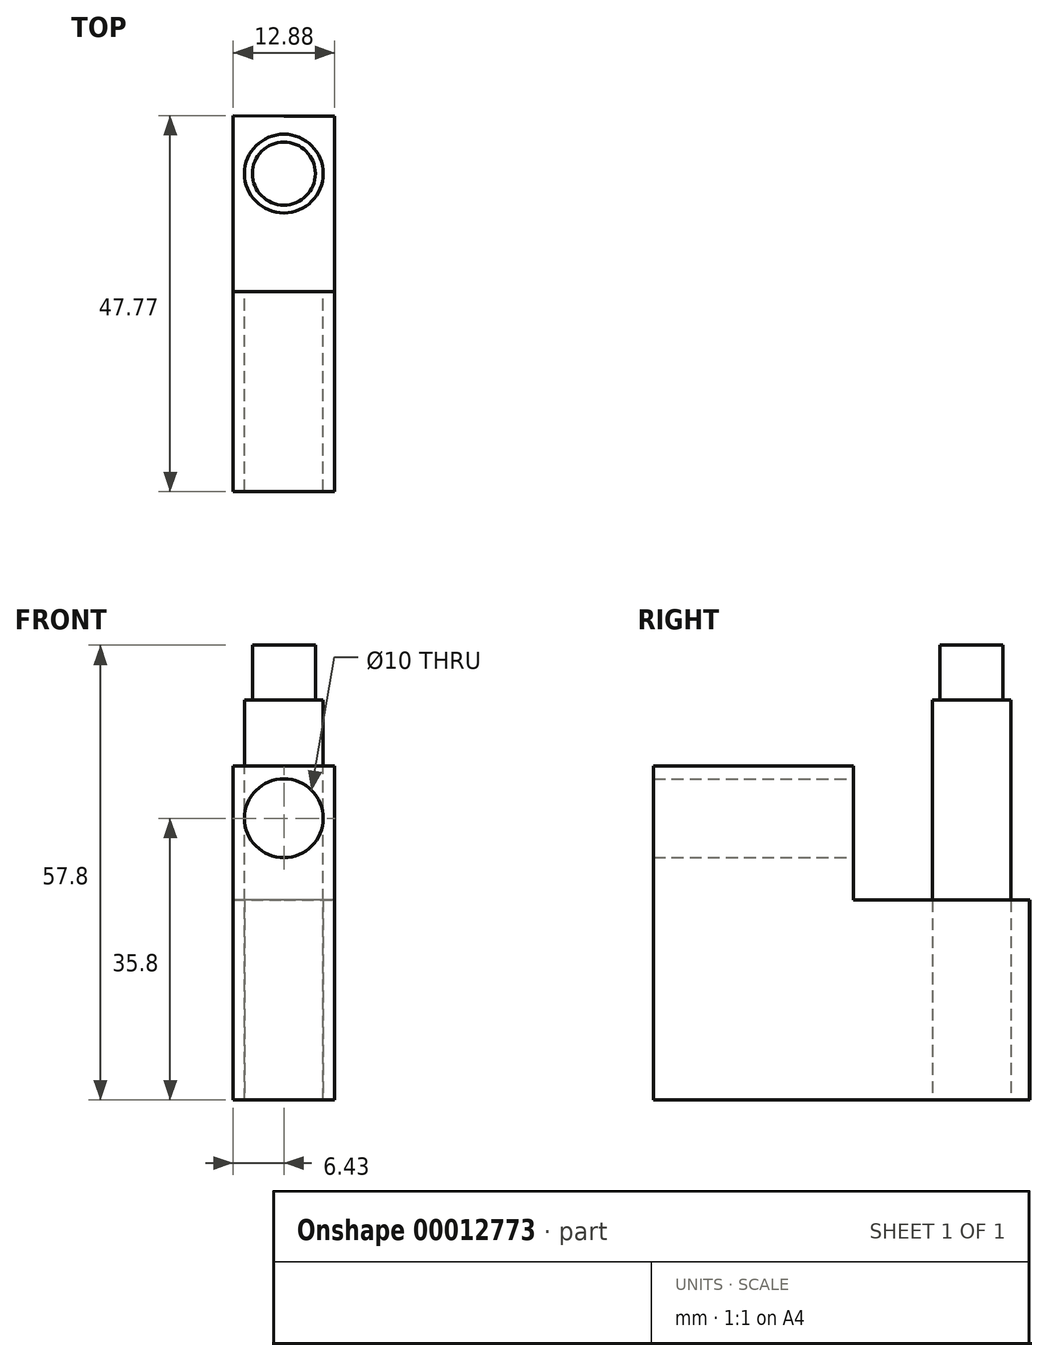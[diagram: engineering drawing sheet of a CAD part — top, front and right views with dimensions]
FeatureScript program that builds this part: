
annotation { "Feature Type Name" : "Feature", "Feature Type Description" : "" }
export const myFeature = defineFeature(function(context is Context, id is Id, definition is map)
    precondition{}
    {
        {
            var Q0;
            Q0=qCreatedBy(makeId("Top.planeOp"),FACE);
            var sketch = newSketch(context, id + "F0", { "sketchPlane" : qUnion([Q0])});
            skCircle(sketch, "E0", {"center": v(0, 0) * mm, "radius": 4 * mm});
            skSolve(sketch);
        }
        {
            var Q0;
            Q0=makeQuery(id+"F0.imprint","IMPRINT",FACE,{"disambiguationData":[TD([[makeQuery(id+"F0.imprint","IMPRINT",EDGE,{"derivedFrom":sQuery(id+"F0.wireOp",EDGE,"E0")}),1.0]])]});
            extrude(context, id + "F1", {"entities" : qUnion([Q0]), "depth" : 7 * mm});
        }
        {
            var Q0;
            Q0=qCreatedBy(makeId("Top.planeOp"),FACE);
            var sketch = newSketch(context, id + "F2", { "sketchPlane" : qUnion([Q0])});
            skCircle(sketch, "E1", {"center": v(0, 0) * mm, "radius": 5 * mm});
            skSolve(sketch);
        }
        {
            var Q0;
            Q0=makeQuery(id+"F2.imprint","IMPRINT",FACE,{"disambiguationData":[TD([[makeQuery(id+"F2.imprint","IMPRINT",EDGE,{"derivedFrom":sQuery(id+"F2.wireOp",EDGE,"E1")}),1.0]])]});
            extrude(context, id + "F3", {"entities" : qUnion([Q0]), "operationType" : NewBodyOperationType.ADD, "oppositeDirection" : true, "depth" : 50.8 * mm});
        }
        {
            var Q0;
            Q0=makeQuery(id+"F3.opExtrude","CAP_FACE",FACE,{"disambiguationData":[OSD([sQuery(id+"F2.wireOp",EDGE,"E1")])],"isStart":false});
            var sketch = newSketch(context, id + "F4", { "sketchPlane" : qUnion([Q0])});
            skLineSegment(sketch, "E2", {"start": v(0, -7.31) * mm, "end": v(6.45, -7.31) * mm});
            skLineSegment(sketch, "E3", {"start": v(6.45, -7.31) * mm, "end": v(6.45, 15) * mm});
            skLineSegment(sketch, "E4", {"start": v(6.45, 15) * mm, "end": v(-6.43, 15) * mm});
            skLineSegment(sketch, "E5", {"start": v(-6.43, 15) * mm, "end": v(-6.43, -7.37) * mm});
            skLineSegment(sketch, "E6", {"start": v(-6.43, -7.37) * mm, "end": v(0, -7.31) * mm});
            skCircle(sketch, "E7", {"center": v(0, 0) * mm, "radius": 5 * mm});
            skSolve(sketch);
        }
        {
            var Q0;
            Q0=makeQuery(id+"F4.imprint","IMPRINT",FACE,{"disambiguationData":[TD([[makeQuery(id+"F4.imprint","IMPRINT",EDGE,{"derivedFrom":sQuery(id+"F4.wireOp",EDGE,"E2")}),1.0]])]});
            extrude(context, id + "F5", {"entities" : qUnion([Q0]), "oppositeDirection" : true, "depth" : 25.4 * mm});
        }
        {
            var Q0;
            Q0=makeQuery(id+"F5.opExtrude","SWEPT_FACE",FACE,{"disambiguationData":[OSD([sQuery(id+"F4.wireOp",EDGE,"E4")])]});
            var sketch = newSketch(context, id + "F6", { "sketchPlane" : qUnion([Q0])});
            skCircle(sketch, "E8", {"center": v(0, -15) * mm, "radius": 5 * mm});
            skLineSegment(sketch, "E9", {"start": v(-6.43, -50.8) * mm, "end": v(-6.43, -8.33) * mm});
            skLineSegment(sketch, "E10", {"start": v(-6.43, -8.33) * mm, "end": v(6.45, -8.33) * mm});
            skLineSegment(sketch, "E11", {"start": v(-6.43, -50.8) * mm, "end": v(6.45, -50.8) * mm});
            skLineSegment(sketch, "E12", {"start": v(6.45, -50.8) * mm, "end": v(6.45, -8.33) * mm});
            skSolve(sketch);
        }
        {
            var Q0;
            {var subQ4=sQuery(id+"F6.wireOp",EDGE,"E11");Q0=qUnion([makeQuery(id+"F6.imprint","IMPRINT",FACE,{"disambiguationData":[TD([[makeQuery(id+"F6.imprint","IMPRINT",EDGE,{"derivedFrom":subQ4}),-1.0]])]}),makeQuery(id+"F6.imprint","IMPRINT",FACE,{"disambiguationData":[TD([[makeQuery(id+"F6.imprint","IMPRINT",EDGE,{"derivedFrom":sQuery(id+"F6.wireOp",EDGE,"E8")}),-1.0]])]})]);}
            extrude(context, id + "F7", {"entities" : qUnion([Q0]), "operationType" : NewBodyOperationType.ADD, "depth" : 25.4 * mm});
        }
    });
